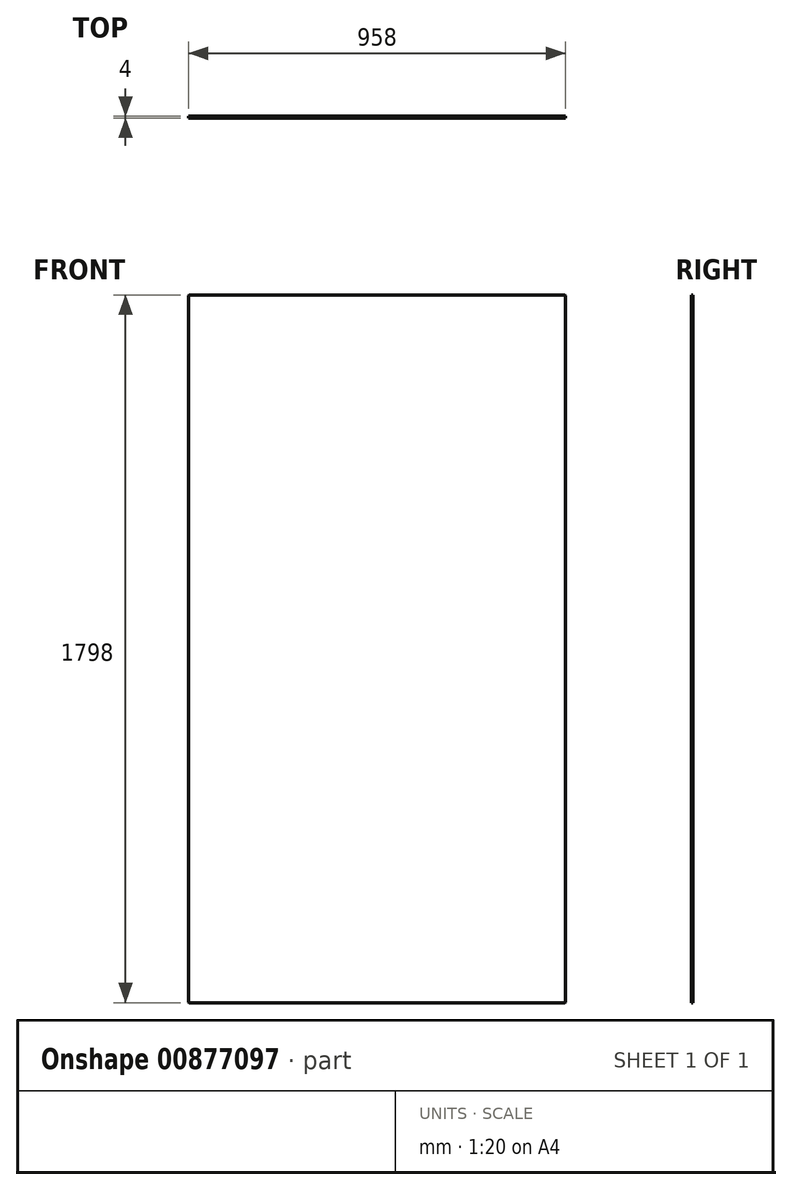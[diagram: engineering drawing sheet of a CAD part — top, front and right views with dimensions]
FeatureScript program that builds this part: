
annotation { "Feature Type Name" : "Feature", "Feature Type Description" : "" }
export const myFeature = defineFeature(function(context is Context, id is Id, definition is map)
    precondition{}
    {
        {
            var Q0;
            Q0=qCreatedBy(makeId("Front.planeOp"),FACE);
            var sketch = newSketch(context, id + "F0", { "sketchPlane" : qUnion([Q0])});
            skLineSegment(sketch, "E0.bottom", {"start": v(479, -899) * mm, "end": v(-479, -899) * mm});
            skLineSegment(sketch, "E0.top", {"start": v(479, 899) * mm, "end": v(-479, 899) * mm});
            skLineSegment(sketch, "E0.left", {"start": v(479, -899) * mm, "end": v(479, 899) * mm});
            skLineSegment(sketch, "E0.right", {"start": v(-479, -899) * mm, "end": v(-479, 899) * mm});
            skPoint(sketch, "E0.middle", {"position": v(0, 0) * mm});
            skSolve(sketch);
        }
        {
            var Q0;
            Q0=makeQuery(id+"F0.imprint","IMPRINT",FACE,{"disambiguationData":[TD([[makeQuery(id+"F0.imprint","IMPRINT",EDGE,{"derivedFrom":sQuery(id+"F0.wireOp",EDGE,"E0.bottom")}),-1.0]])]});
            extrude(context, id + "F1", {"entities" : qUnion([Q0]), "endBound" : BoundingType.SYMMETRIC, "depth" : 4 * mm, "offsetDistance" : 25 * mm});
        }
        {
            var Q0;
            Q0=makeQuery(id+"F1.opExtrude","SWEPT_EDGE",EDGE,{"disambiguationData":[OSD([sQuery(id+"F0.wireOp",EDGE,"E0.top"),sQuery(id+"F0.wireOp",EDGE,"E0.left")])]});
            var Q1;
            Q1=makeQuery(id+"F1.opExtrude","SWEPT_EDGE",EDGE,{"disambiguationData":[OSD([sQuery(id+"F0.wireOp",EDGE,"E0.top"),sQuery(id+"F0.wireOp",EDGE,"E0.right")])]});
            var Q2;
            Q2=makeQuery(id+"F1.opExtrude","SWEPT_EDGE",EDGE,{"disambiguationData":[OSD([sQuery(id+"F0.wireOp",EDGE,"E0.bottom"),sQuery(id+"F0.wireOp",EDGE,"E0.right")])]});
            var Q3;
            Q3=makeQuery(id+"F1.opExtrude","SWEPT_EDGE",EDGE,{"disambiguationData":[OSD([sQuery(id+"F0.wireOp",EDGE,"E0.bottom"),sQuery(id+"F0.wireOp",EDGE,"E0.left")])]});
            chamfer(context, id + "F2", {"entities" : qUnion([Q0, Q1, Q2, Q3]), "width" : 1 * mm, "tangentPropagation" : true});
        }
    });
